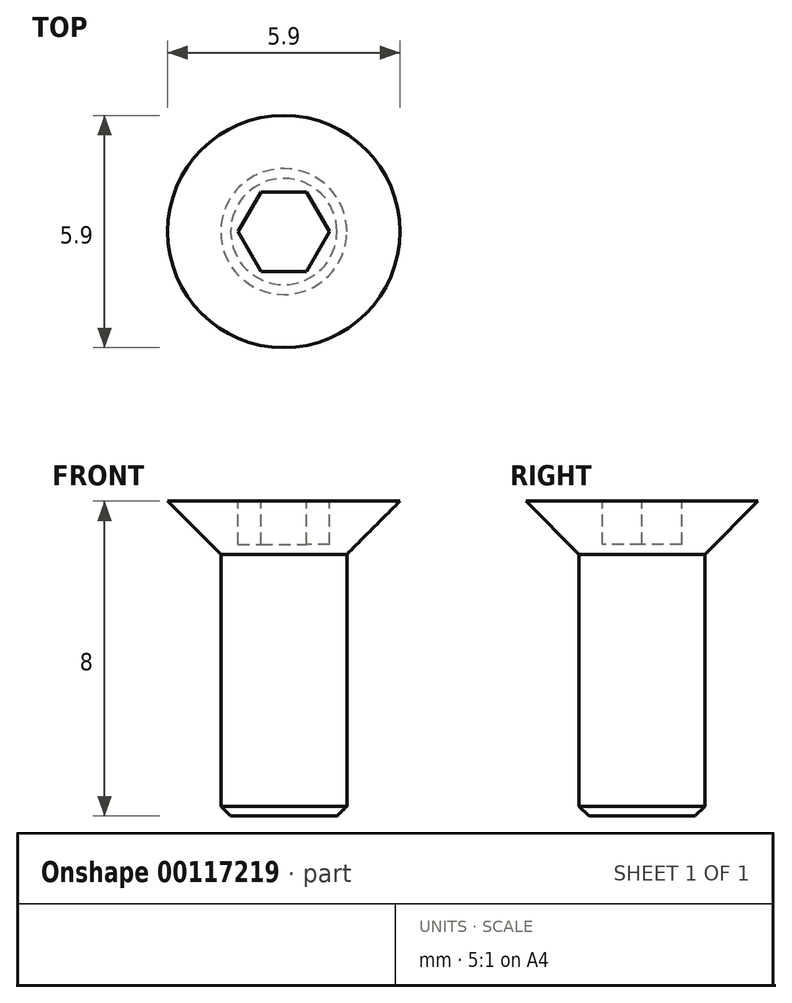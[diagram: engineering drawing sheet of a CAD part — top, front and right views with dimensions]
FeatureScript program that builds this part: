
annotation { "Feature Type Name" : "Feature", "Feature Type Description" : "" }
export const myFeature = defineFeature(function(context is Context, id is Id, definition is map)
    precondition{}
    {
        {
            var Q0;
            Q0=qCreatedBy(makeId("Front.planeOp"),FACE);
            var sketch = newSketch(context, id + "F0", { "sketchPlane" : qUnion([Q0])});
            skLineSegment(sketch, "E0.top", {"start": v(0, -4.24) * mm, "end": v(-1.6, -4.24) * mm});
            skLineSegment(sketch, "E0.left", {"start": v(0, 3.76) * mm, "end": v(0, -4.24) * mm});
            skLineSegment(sketch, "E0.right", {"start": v(-1.6, 2.4) * mm, "end": v(-1.6, -4.24) * mm});
            skLineSegment(sketch, "E1", {"start": v(-1.6, 2.4) * mm, "end": v(-2.95, 3.76) * mm});
            skLineSegment(sketch, "E2", {"start": v(-2.95, 3.76) * mm, "end": v(0, 3.76) * mm});
            skPoint(sketch, "E3.orphan", {"position": v(0, 2.76) * mm});
            skSolve(sketch);
        }
        {
            var Q0;
            Q0=makeQuery(id+"F0.imprint","IMPRINT",FACE,{"disambiguationData":[TD([[makeQuery(id+"F0.imprint","IMPRINT",EDGE,{"derivedFrom":sQuery(id+"F0.wireOp",EDGE,"E0.top")}),-1.0]])]});
            var Q1;
            Q1=sQuery(id+"F0.wireOp",EDGE,"E0.left");
            revolve(context, id + "F1", {"entities" : qUnion([Q0]), "axis" : qUnion([Q1]), "revolveType" : RevolveType.FULL});
        }
        {
            var Q0;
            Q0=makeQuery(id+"F1.opRevolve","SWEPT_FACE",FACE,{"disambiguationData":[OSD([sQuery(id+"F0.wireOp",EDGE,"E2")])]});
            var sketch = newSketch(context, id + "F2", { "sketchPlane" : qUnion([Q0])});
            skCircle(sketch, "E4.cCircle", {"center": v(0, 0) * mm, "radius": 1.01 * mm, "construction": true});
            skLineSegment(sketch, "E4.0", {"start": v(1.17, 0) * mm, "end": v(0.58, -1.01) * mm});
            skLineSegment(sketch, "E4.1", {"start": v(0.58, -1) * mm, "end": v(-0.58, -1) * mm});
            skLineSegment(sketch, "E4.2", {"start": v(-0.58, -1) * mm, "end": v(-1.17, 0) * mm});
            skLineSegment(sketch, "E4.3", {"start": v(-1.17, 0) * mm, "end": v(-0.58, 1.01) * mm});
            skLineSegment(sketch, "E4.4", {"start": v(-0.58, 1) * mm, "end": v(0.58, 1) * mm});
            skLineSegment(sketch, "E4.5", {"start": v(0.58, 1) * mm, "end": v(1.17, 0) * mm});
            skPoint(sketch, "E4.0.midPoint", {"position": v(0.87, -0.5) * mm});
            skSolve(sketch);
        }
        {
            var Q0;
            Q0=makeQuery(id+"F2.imprint","IMPRINT",FACE,{"disambiguationData":[TD([[makeQuery(id+"F2.imprint","IMPRINT",EDGE,{"derivedFrom":sQuery(id+"F2.wireOp",EDGE,"E4.0")}),-1.0]])]});
            extrude(context, id + "F3", {"entities" : qUnion([Q0]), "operationType" : NewBodyOperationType.REMOVE, "oppositeDirection" : true, "depth" : 1.1 * mm});
        }
        {
            var Q0;
            Q0=makeQuery(id+"F1.opRevolve","SWEPT_EDGE",EDGE,{"disambiguationData":[OSD([sQuery(id+"F0.wireOp",EDGE,"E0.top"),sQuery(id+"F0.wireOp",EDGE,"E0.right")])]});
            chamfer(context, id + "F4", {"entities" : qUnion([Q0]), "width" : .25 * mm, "tangentPropagation" : true});
        }
    });
